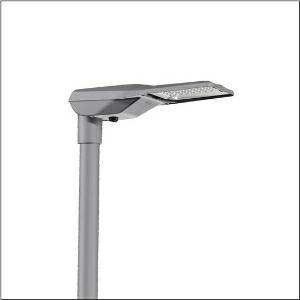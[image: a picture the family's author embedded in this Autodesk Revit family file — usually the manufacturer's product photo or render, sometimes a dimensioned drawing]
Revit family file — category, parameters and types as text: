
# Revit family: streetlight_sl_21_mini___p0_5a_5xe2v33r08jb_a833
name_source: partatom
category: Lighting Fixtures
units: mm (PartAtom-declared; Revit-internal decimal feet)

## family parameters
Cut with Voids When Loaded = No
Host = Face
Light Source = No
Part Type = Normal
Room Calculation Point = No
Round Connector Dimension = Use Diameter
Shared = No

## types (1)
- --- (1 x LED, 12720 lm, 88.6 W, 3000K)
    Apparent Load = 89 VA
    CIE Flux Codes = 37 73 96 100 100
    Color Rendering = 70
    Color Temperature = 3000K
    Default Elevation = 1800 mm
    Description = Streetlight SL 21 mini, mast luminaire, primary light control with lens, of PMMA, primary optical cover: cover, of toughened safety glass, transparent, light distribution: P0.5a, light emission: direct distribution, primary light characteristic: asymmetric, installation type: post-top, side-entry, LED, High Power LED, rated luminous flux: 12.720lm, luminous efficacy: 144lm/W, light colour: 730, colour temperature: 3000K, control gear: D4i, control: pre-setting: logarithmic dimming characteristic, flexible luminous flux parameterisation, time-dependent luminous flux control, constant luminous flux control, overheat protection, mains connection: 220..240V, AC, 50/60Hz, start of lifetime: 89W, end of service life: 92W, reduction: 41W, luminaire housing, of diecast aluminium, powder-coated, Siteco® metallic grey (DB 702S), corrosivity category C5 mid according to DIN EN ISO 12944, multi-level sealing system, sealing non-destructively replaceable, inclination adjustable: 0°, 5°, 10°, 15°, please order mast flange separately, length: 628mm, width: 235mm, height: 110mm, mast flange for spigot size: 42mm (side-entry): 5XC10008XM4, 60/48mm (side-entry/post-top): 5XC10108XM2, 76/60mm (side-entry/post-top): 5XC10108XM1, mounting height: 4..8m, Smart Interface below, protection rating (complete): IP66, insulation class (complete): insulation class II (safety insulation), certification: CE, ENEC, ENEC+, VDE, impact resistance: IK10, permissible operating ambient temperature for outdoor applications: -40..+50°C, standard-compliant lighting for roads and squares, packaging unit: 1 piece

Light Distribution: P0.5a
    Height = 110 mm
    Lamp = 1 x LED
    Lamp Light Flux = 12720 lm
    Lamp Power = 88.6 W
    Lamp count = 1
    Length = 625 mm
    Luminous efficacy = 144 lm/W
    Manufacturer = Siteco
    ModVariant = No
    Model = 5XE2V33R08JB
    Number of Poles = 1
    OnlyDefault = Yes
    Power Factor = 1
    Product Name = Streetlight SL 21 mini | P0.5a
    Product group = mast luminaire | pylon top
    ProductGroupID = 6100
    Protection Class = Protection class II
    Protection Degree = IP 66
    RLX_Detail_Level = 1
    RLX_Emergency_Light_Flux = 0 lm
    RLX_Emergency_Type = 0
    RLX_Emergency_Type_DB = No
    RlxData = <blob elided: 26065 chars, md5=7c55ae0b>
    Socket = socket
    Standby Power = 0 W
    System Light Flux = 12720 lm
    System Power = 89 W
    Type Comments = factory setting: luminous flux: 100 % | dim-lin: 254 | 915 mA
    Type Image = l_1003516.jpg
    URL = http://relux.com
    VarID = @adj_033015
    Voltage = 0 V
    Weight = 0.00 kg
    Width = 234 mm

## geometry (parser evidence)
native form markers: Blend x4, Sweep x12
no freeform markers — native parametric forms only
